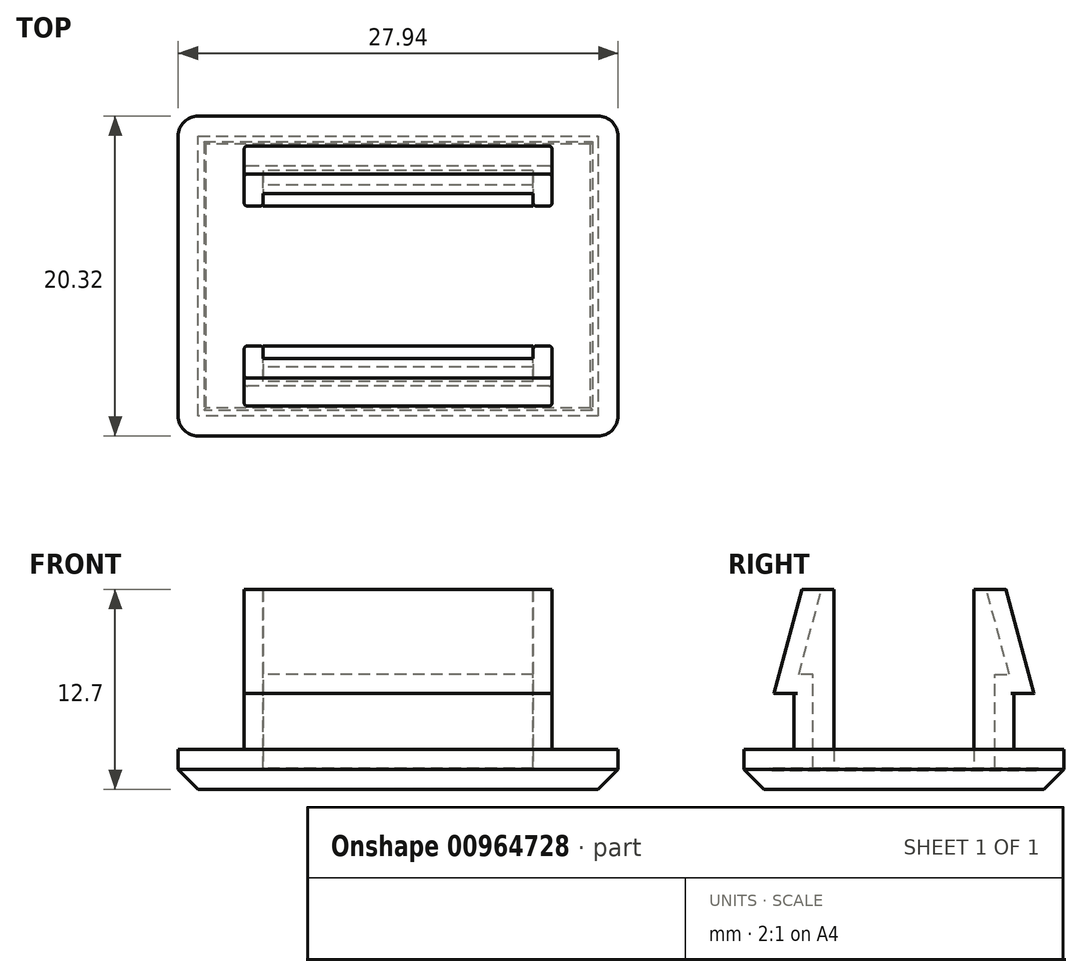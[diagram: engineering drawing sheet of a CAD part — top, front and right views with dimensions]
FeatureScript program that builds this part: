
annotation { "Feature Type Name" : "Feature", "Feature Type Description" : "" }
export const myFeature = defineFeature(function(context is Context, id is Id, definition is map)
    precondition{}
    {
        {
            var Q0;
            Q0=qCreatedBy(makeId("Top.planeOp"),FACE);
            var sketch = newSketch(context, id + "F0", { "sketchPlane" : qUnion([Q0])});
            skLineSegment(sketch, "E0.bottom", {"start": v(13.97, -10.16) * mm, "end": v(-13.97, -10.16) * mm});
            skLineSegment(sketch, "E0.top", {"start": v(13.97, 10.16) * mm, "end": v(-13.97, 10.16) * mm});
            skLineSegment(sketch, "E0.left", {"start": v(13.97, -10.16) * mm, "end": v(13.97, 10.16) * mm});
            skLineSegment(sketch, "E0.right", {"start": v(-13.97, -10.16) * mm, "end": v(-13.97, 10.16) * mm});
            skPoint(sketch, "E0.middle", {"position": v(0, 0) * mm});
            skSolve(sketch);
        }
        {
            var Q0;
            Q0 = qSketchRegion(id + "F0", true);
            extrude(context, id + "F1", {"entities" : qUnion([Q0]), "depth" : 2.54 * mm, "offsetDistance" : 25.4 * mm});
        }
        {
            var Q0;
            Q0=qCreatedBy(makeId("Right.planeOp"),FACE);
            var sketch = newSketch(context, id + "F2", { "sketchPlane" : qUnion([Q0])});
            skLineSegment(sketch, "E1", {"start": v(0, 2.54) * mm, "end": v(0, 14.5) * mm, "construction": true});
            skLineSegment(sketch, "E2", {"start": v(-6.99, 2.54) * mm, "end": v(-6.99, 6.1) * mm});
            skLineSegment(sketch, "E3", {"start": v(-6.99, 6.1) * mm, "end": v(-8.26, 6.1) * mm});
            skLineSegment(sketch, "E4", {"start": v(-8.26, 6.1) * mm, "end": v(-6.48, 12.7) * mm});
            skLineSegment(sketch, "E5", {"start": v(-6.48, 12.7) * mm, "end": v(-4.45, 12.7) * mm});
            skLineSegment(sketch, "E6", {"start": v(-4.45, 12.7) * mm, "end": v(-4.44, 2.54) * mm});
            skLineSegment(sketch, "E7", {"start": v(-4.44, 2.54) * mm, "end": v(-6.99, 2.54) * mm});
            skLineSegment(sketch, "E8.MirrorCS", {"start": v(6.48, 12.7) * mm, "end": v(4.44, 12.7) * mm});
            skLineSegment(sketch, "E9.MirrorCS", {"start": v(6.99, 6.1) * mm, "end": v(8.26, 6.1) * mm});
            skLineSegment(sketch, "E10.MirrorCS", {"start": v(8.26, 6.1) * mm, "end": v(6.48, 12.7) * mm});
            skLineSegment(sketch, "E11.MirrorCS", {"start": v(4.45, 2.54) * mm, "end": v(6.99, 2.54) * mm});
            skLineSegment(sketch, "E12.MirrorCS", {"start": v(4.45, 12.7) * mm, "end": v(4.45, 2.54) * mm});
            skLineSegment(sketch, "E13.MirrorCS", {"start": v(6.99, 2.54) * mm, "end": v(6.99, 6.1) * mm});
            skSolve(sketch);
        }
        {
            var Q0;
            Q0 = qSketchRegion(id + "F2", true);
            extrude(context, id + "F3", {"entities" : qUnion([Q0]), "operationType" : NewBodyOperationType.ADD, "endBound" : BoundingType.SYMMETRIC, "depth" : 19.56 * mm, "offsetDistance" : 25.4 * mm});
        }
        {
            var Q0;
            Q0=makeQuery(id+"F1.opExtrude","SWEPT_EDGE",EDGE,{"disambiguationData":[OSD([sQuery(id+"F0.wireOp",EDGE,"E0.bottom"),sQuery(id+"F0.wireOp",EDGE,"E0.left")])]});
            var Q1;
            Q1=makeQuery(id+"F1.opExtrude","SWEPT_EDGE",EDGE,{"disambiguationData":[OSD([sQuery(id+"F0.wireOp",EDGE,"E0.top"),sQuery(id+"F0.wireOp",EDGE,"E0.left")])]});
            var Q2;
            Q2=makeQuery(id+"F1.opExtrude","SWEPT_EDGE",EDGE,{"disambiguationData":[OSD([sQuery(id+"F0.wireOp",EDGE,"E0.top"),sQuery(id+"F0.wireOp",EDGE,"E0.right")])]});
            var Q3;
            Q3=makeQuery(id+"F1.opExtrude","SWEPT_EDGE",EDGE,{"disambiguationData":[OSD([sQuery(id+"F0.wireOp",EDGE,"E0.bottom"),sQuery(id+"F0.wireOp",EDGE,"E0.right")])]});
            fillet(context, id + "F4", {"entities" : qUnion([Q0, Q1, Q2, Q3]), "radius" : 1.27 * mm, "tangentPropagation" : true, "allowEdgeOverflow" : false});
        }
        {
            var Q0;
            Q0=makeQuery(id+"F1.opExtrude","CAP_FACE",FACE,{"disambiguationData":[OSD([sQuery(id+"F0.wireOp",EDGE,"E0.bottom"),sQuery(id+"F0.wireOp",EDGE,"E0.top"),sQuery(id+"F0.wireOp",EDGE,"E0.left"),sQuery(id+"F0.wireOp",EDGE,"E0.right")])],"isStart":true});
            chamfer(context, id + "F5", {"entities" : qUnion([Q0]), "width" : 1.27 * mm, "tangentPropagation" : true});
        }
        {
            var Q0;
            Q0=makeQuery(id+"F3.opExtrude","SWEPT_FACE",FACE,{"disambiguationData":[OSD([sQuery(id+"F2.wireOp",EDGE,"E6")])]});
            var Q1;
            Q1=makeQuery(id+"F3.opExtrude","SWEPT_FACE",FACE,{"disambiguationData":[OSD([sQuery(id+"F2.wireOp",EDGE,"E5")])]});
            var Q2;
            Q2=makeQuery(id+"F3.opExtrude","SWEPT_FACE",FACE,{"disambiguationData":[OSD([sQuery(id+"F2.wireOp",EDGE,"E12.MirrorCS")])]});
            var Q3;
            Q3=makeQuery(id+"F3.opExtrude","SWEPT_FACE",FACE,{"disambiguationData":[OSD([sQuery(id+"F2.wireOp",EDGE,"E8.MirrorCS")])]});
            shell(context, id + "F6", {"entities" : qUnion([Q0, Q1, Q2, Q3]), "thickness" : 1.2 * mm});
        }
        {
            var Q0;
            Q0=makeQuery(id+"F3.opExtrude","CAP_EDGE",EDGE,{"disambiguationData":[OSD([sQuery(id+"F2.wireOp",EDGE,"E12.MirrorCS")])],"isStart":true});
            var Q1;
            {var subQ0=sQuery(id+"F2.wireOp",EDGE,"E12.MirrorCS");Q1=makeQuery(id+"F6.opShell","OFFSET_EDGE",EDGE,{"disambiguationData":[OSD([subQ0]),TDD([makeQuery(id+"F3.opExtrude","CAP_EDGE",EDGE,{"disambiguationData":[OSD([subQ0])],"isStart":true})]),OD(0.0)]});}
            var Q2;
            {var subQ0=sQuery(id+"F2.wireOp",EDGE,"E12.MirrorCS");Q2=makeQuery(id+"F6.opShell","OFFSET_EDGE",EDGE,{"disambiguationData":[OSD([subQ0]),TDD([makeQuery(id+"F3.opExtrude","CAP_EDGE",EDGE,{"disambiguationData":[OSD([subQ0])],"isStart":false})]),OD(0.0)]});}
            var Q3;
            Q3=makeQuery(id+"F3.opExtrude","CAP_EDGE",EDGE,{"disambiguationData":[OSD([sQuery(id+"F2.wireOp",EDGE,"E12.MirrorCS")])],"isStart":false});
            var Q4;
            Q4=makeQuery(id+"F3.opExtrude","CAP_EDGE",EDGE,{"disambiguationData":[OSD([sQuery(id+"F2.wireOp",EDGE,"E13.MirrorCS")])],"isStart":false});
            var Q5;
            Q5=makeQuery(id+"F3.opExtrude","CAP_EDGE",EDGE,{"disambiguationData":[OSD([sQuery(id+"F2.wireOp",EDGE,"E10.MirrorCS")])],"isStart":false});
            var Q6;
            Q6=makeQuery(id+"F3.opExtrude","CAP_EDGE",EDGE,{"disambiguationData":[OSD([sQuery(id+"F2.wireOp",EDGE,"E13.MirrorCS")])],"isStart":true});
            var Q7;
            Q7=makeQuery(id+"F3.opExtrude","CAP_EDGE",EDGE,{"disambiguationData":[OSD([sQuery(id+"F2.wireOp",EDGE,"E10.MirrorCS")])],"isStart":true});
            var Q8;
            Q8=makeQuery(id+"F3.opExtrude","CAP_EDGE",EDGE,{"disambiguationData":[OSD([sQuery(id+"F2.wireOp",EDGE,"E6")])],"isStart":true});
            var Q9;
            {var subQ0=sQuery(id+"F2.wireOp",EDGE,"E6");Q9=makeQuery(id+"F6.opShell","OFFSET_EDGE",EDGE,{"disambiguationData":[OSD([subQ0]),TDD([makeQuery(id+"F3.opExtrude","CAP_EDGE",EDGE,{"disambiguationData":[OSD([subQ0])],"isStart":true})]),OD(0.0)]});}
            var Q10;
            Q10=makeQuery(id+"F3.opExtrude","CAP_EDGE",EDGE,{"disambiguationData":[OSD([sQuery(id+"F2.wireOp",EDGE,"E2")])],"isStart":true});
            var Q11;
            Q11=makeQuery(id+"F3.opExtrude","CAP_EDGE",EDGE,{"disambiguationData":[OSD([sQuery(id+"F2.wireOp",EDGE,"E4")])],"isStart":true});
            var Q12;
            Q12=makeQuery(id+"F3.opExtrude","CAP_EDGE",EDGE,{"disambiguationData":[OSD([sQuery(id+"F2.wireOp",EDGE,"E2")])],"isStart":false});
            var Q13;
            Q13=makeQuery(id+"F3.opExtrude","CAP_EDGE",EDGE,{"disambiguationData":[OSD([sQuery(id+"F2.wireOp",EDGE,"E4")])],"isStart":false});
            var Q14;
            Q14=makeQuery(id+"F3.opExtrude","CAP_EDGE",EDGE,{"disambiguationData":[OSD([sQuery(id+"F2.wireOp",EDGE,"E6")])],"isStart":false});
            var Q15;
            {var subQ0=sQuery(id+"F2.wireOp",EDGE,"E6");Q15=makeQuery(id+"F6.opShell","OFFSET_EDGE",EDGE,{"disambiguationData":[OSD([subQ0]),TDD([makeQuery(id+"F3.opExtrude","CAP_EDGE",EDGE,{"disambiguationData":[OSD([subQ0])],"isStart":false})]),OD(0.0)]});}
            fillet(context, id + "F7", {"entities" : qUnion([Q0, Q1, Q2, Q3, Q4, Q5, Q6, Q7, Q8, Q9, Q10, Q11, Q12, Q13, Q14, Q15]), "radius" : .2 * mm, "tangentPropagation" : true, "allowEdgeOverflow" : false});
        }
    });
